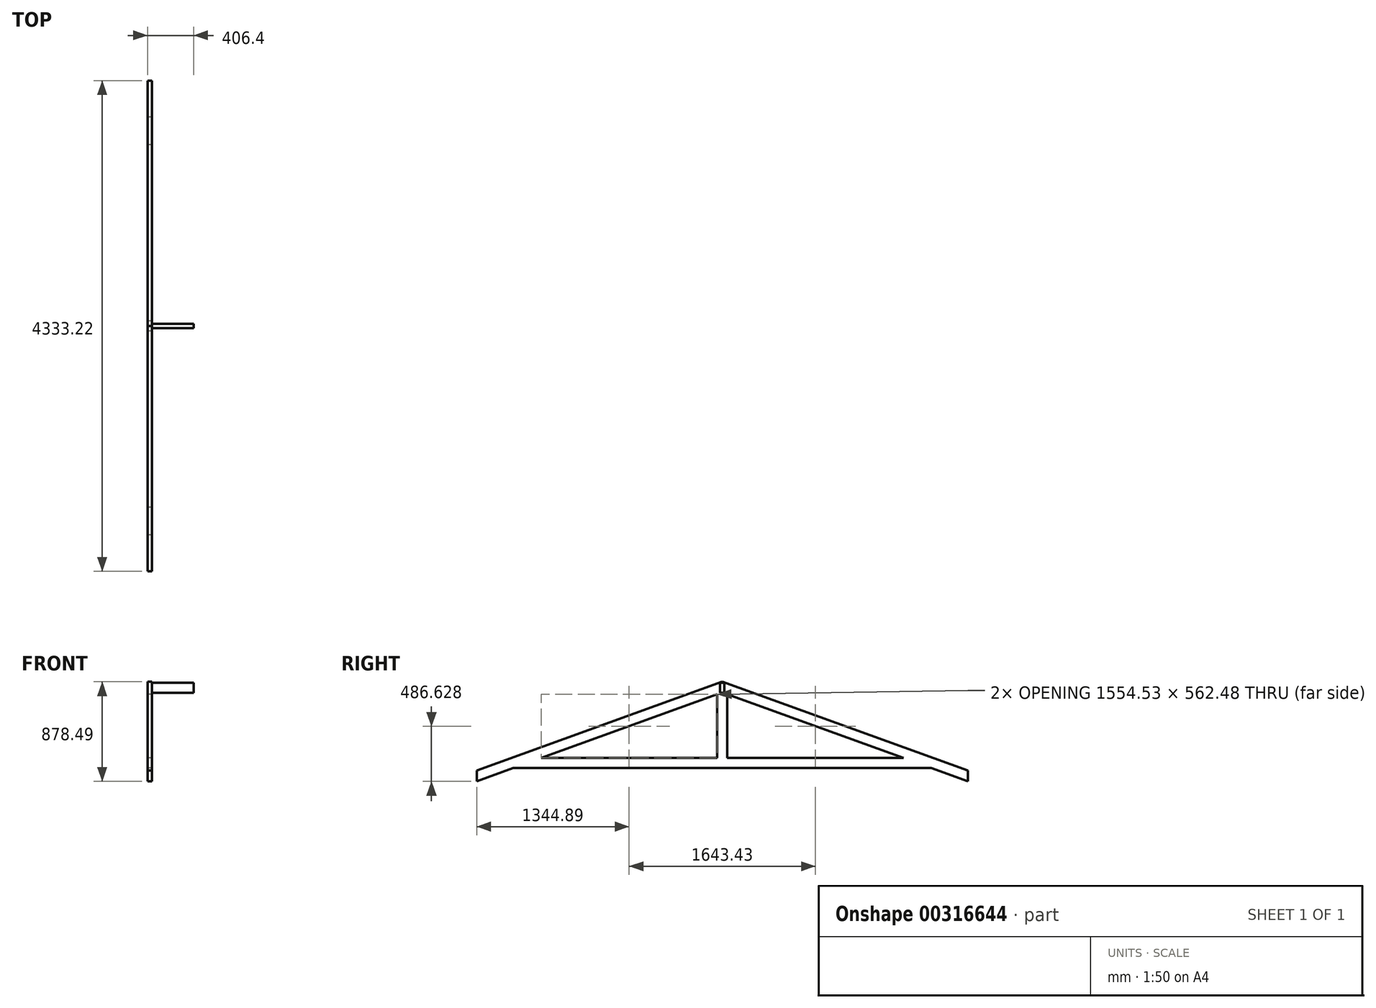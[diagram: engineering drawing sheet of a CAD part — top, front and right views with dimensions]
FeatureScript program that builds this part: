
annotation { "Feature Type Name" : "Feature", "Feature Type Description" : "" }
export const myFeature = defineFeature(function(context is Context, id is Id, definition is map)
    precondition{}
    {
        {
            var Q0;
            Q0=qCreatedBy(makeId("Right.planeOp"),FACE);
            var sketch = newSketch(context, id + "F0", { "sketchPlane" : qUnion([Q0])});
            skLineSegment(sketch, "E0", {"start": v(-1844.68, 0) * mm, "end": v(1844.68, 0) * mm});
            skLineSegment(sketch, "E1", {"start": v(-2166.6, -116.49) * mm, "end": v(0, 667.46) * mm});
            skLineSegment(sketch, "E2", {"start": v(0, 762) * mm, "end": v(-2166.6, -21.94) * mm});
            skLineSegment(sketch, "E3", {"start": v(-2166.6, -21.94) * mm, "end": v(-2166.6, -116.49) * mm});
            skLineSegment(sketch, "E4", {"start": v(0, 667.46) * mm, "end": v(0, 762) * mm});
            skPoint(sketch, "E5.orphan", {"position": v(0, 0) * mm});
            skLineSegment(sketch, "E6.MirrorCS", {"start": v(2166.6, -21.94) * mm, "end": v(2166.6, -116.49) * mm});
            skLineSegment(sketch, "E7.MirrorCS", {"start": v(0, 762) * mm, "end": v(2166.6, -21.94) * mm});
            skLineSegment(sketch, "E8.MirrorCS", {"start": v(2166.6, -116.49) * mm, "end": v(0, 667.46) * mm});
            skLineSegment(sketch, "E9", {"start": v(-1598.98, 88.9) * mm, "end": v(1598.98, 88.9) * mm});
            skLineSegment(sketch, "E10", {"start": v(-44.45, 651.38) * mm, "end": v(-44.45, 88.9) * mm});
            skLineSegment(sketch, "E11", {"start": v(-44.45, 88.9) * mm, "end": v(44.45, 88.9) * mm});
            skLineSegment(sketch, "E12", {"start": v(44.45, 88.9) * mm, "end": v(44.45, 651.38) * mm});
            skPoint(sketch, "E13", {"position": v(0, 88.9) * mm});
            skLineSegment(sketch, "E14", {"start": v(-2166.6, -116.49) * mm, "end": v(-2214.24, 15.16) * mm, "construction": true});
            skSolve(sketch);
        }
        {
            var Q0;
            {var subQ3=sQuery(id+"F0.wireOp",EDGE,"E4");Q0=makeQuery(id+"F0.imprint","IMPRINT",FACE,{"disambiguationData":[TD([[makeQuery(id+"F0.imprint","IMPRINT",EDGE,{"derivedFrom":subQ3}),-1.0]])]});}
            var Q1;
            Q1=makeQuery(id+"F0.imprint","IMPRINT",FACE,{"disambiguationData":[TD([[makeQuery(id+"F0.imprint","IMPRINT",EDGE,{"derivedFrom":sQuery(id+"F0.wireOp",EDGE,"E2")}),1.0]])]});
            var Q2;
            {var subQ0=sQuery(id+"F0.wireOp",EDGE,"E10");Q2=makeQuery(id+"F0.imprint","IMPRINT",FACE,{"disambiguationData":[TD([[makeQuery(id+"F0.imprint","IMPRINT",EDGE,{"derivedFrom":subQ0}),1.0]])]});}
            var Q3;
            {var subQ4=sQuery(id+"F0.wireOp",EDGE,"E0");Q3=makeQuery(id+"F0.imprint","IMPRINT",FACE,{"disambiguationData":[TD([[makeQuery(id+"F0.imprint","IMPRINT",EDGE,{"derivedFrom":subQ4}),1.0]])]});}
            extrude(context, id + "F1", {"entities" : qUnion([Q0, Q1, Q2, Q3]), "depth" : 38.1 * mm});
        }
        {
            var Q0;
            Q0=makeQuery(id+"F1.opExtrude","CAP_FACE",FACE,{"disambiguationData":[OSD([sQuery(id+"F0.wireOp",EDGE,"E0"),sQuery(id+"F0.wireOp",EDGE,"E2"),sQuery(id+"F0.wireOp",EDGE,"E3"),sQuery(id+"F0.wireOp",EDGE,"E6.MirrorCS"),sQuery(id+"F0.wireOp",EDGE,"E7.MirrorCS"),sQuery(id+"F0.wireOp",EDGE,"E8.MirrorCS"),sQuery(id+"F0.wireOp",EDGE,"E1"),sQuery(id+"F0.wireOp",EDGE,"E9"),sQuery(id+"F0.wireOp",EDGE,"E10"),sQuery(id+"F0.wireOp",EDGE,"E12")])],"isStart":false});
            var sketch = newSketch(context, id + "F2", { "sketchPlane" : qUnion([Q0])});
            skLineSegment(sketch, "E15.bottom", {"start": v(-19.05, 755.1) * mm, "end": v(19.05, 755.1) * mm});
            skLineSegment(sketch, "E15.top", {"start": v(-19.05, 666.2) * mm, "end": v(19.05, 666.2) * mm});
            skLineSegment(sketch, "E15.left", {"start": v(-19.05, 755.1) * mm, "end": v(-19.05, 666.2) * mm});
            skLineSegment(sketch, "E15.right", {"start": v(19.05, 755.1) * mm, "end": v(19.05, 666.2) * mm});
            skPoint(sketch, "E15.middle", {"position": v(0, 710.66) * mm});
            skPoint(sketch, "E15.middle.positionSnap0", {"position": v(0, 0) * mm});
            skPoint(sketch, "E15.centerSnap0", {"position": v(0, 0) * mm});
            skSolve(sketch);
        }
        {
            var Q0;
            Q0=makeQuery(id+"F2.imprint","IMPRINT",FACE,{"disambiguationData":[TD([[makeQuery(id+"F2.imprint","IMPRINT",EDGE,{"derivedFrom":sQuery(id+"F2.wireOp",EDGE,"E15.bottom")}),-1.0]])]});
            extrude(context, id + "F3", {"entities" : qUnion([Q0]), "depth" : 368.3 * mm});
        }
    });
